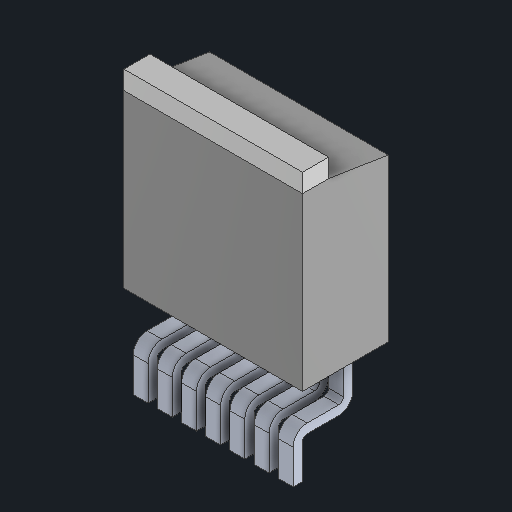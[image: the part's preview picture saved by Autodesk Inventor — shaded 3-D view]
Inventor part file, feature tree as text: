
AUTODESK INVENTOR PART (.ipt)
format: ipt  version: 2024 (Build 280153000, 153)  size: 179,200 bytes
history: native  units: mm
features: other x17, fillet x1
ambient origin geometry x8: Origin, YZ Plane, XZ Plane, XY Plane, X Axis, Y Axis, Z Axis, Center Point
bodies: Body1 (feature_tree), Body2 (feature_tree), Body3 (feature_tree), Body4 (feature_tree), Body5 (feature_tree), Body6 (feature_tree), Body7 (feature_tree), Body8 (feature_tree), Body9 (feature_tree)
feature tree (18):
  other  "Твердое тело1"
  other  "Твердое тело2"
  other  "Твердое тело3"
  other  "Твердое тело4"
  other  "Твердое тело5"
  other  "Твердое тело6"
  other  "Твердое тело7"
  other  "Твердое тело8"
  other  "Твердое тело9"
  other  "Boss-Extrude1"
  other  "Boss-Extrude2"
  fillet  "Fillet2"  [1 undecoded]
  other  "LPattern3[1]"
  other  "LPattern3[2]"
  other  "LPattern3[3]"
  other  "LPattern3[4]"
  other  "LPattern3[5]"
  other  "LPattern3[6]"
note: 1 required parameter value undecoded (feature->parameter linkage not recoverable at this tier; creation-order binding heuristic only, values carry confidence <= 0.55)
